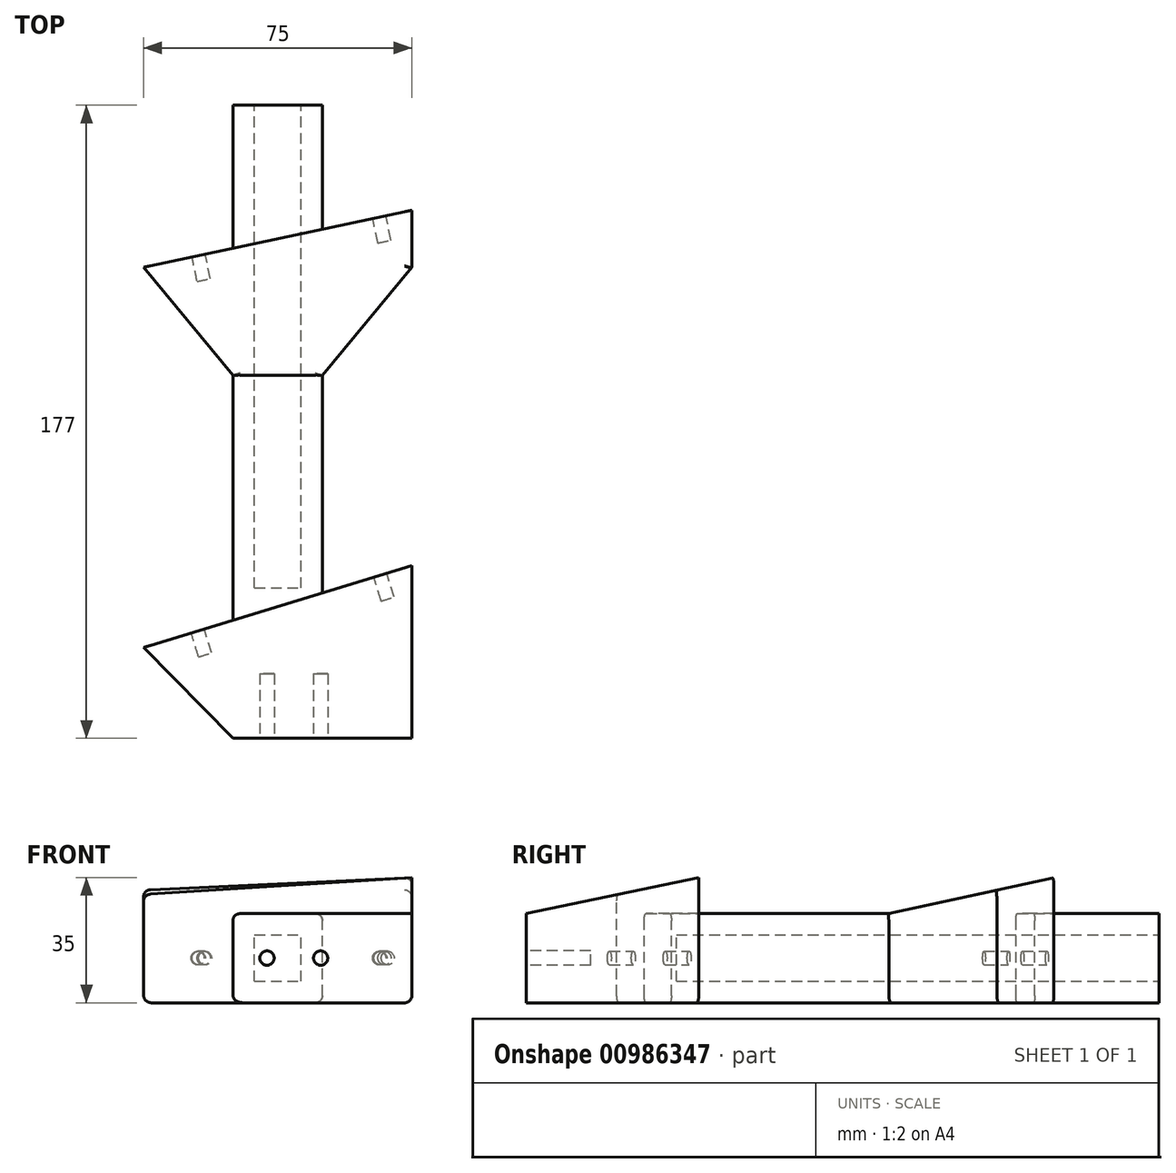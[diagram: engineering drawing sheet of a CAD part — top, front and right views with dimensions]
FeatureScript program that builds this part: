
annotation { "Feature Type Name" : "Feature", "Feature Type Description" : "" }
export const myFeature = defineFeature(function(context is Context, id is Id, definition is map)
    precondition{}
    {
        {
            var Q0;
            Q0=qCreatedBy(makeId("Top.planeOp"),FACE);
            var sketch = newSketch(context, id + "F0", { "sketchPlane" : qUnion([Q0])});
            skLineSegment(sketch, "E0.bottom", {"start": v(0, 0) * mm, "end": v(50, 0) * mm});
            skLineSegment(sketch, "E0.top", {"start": v(0, 33) * mm, "end": v(50, 33) * mm});
            skLineSegment(sketch, "E0.left", {"start": v(0, 0) * mm, "end": v(0, 33) * mm});
            skLineSegment(sketch, "E0.right", {"start": v(50, 0) * mm, "end": v(50, 33) * mm});
            skLineSegment(sketch, "E1", {"start": v(0, 33) * mm, "end": v(50, 48.29) * mm});
            skLineSegment(sketch, "E2", {"start": v(50, 33) * mm, "end": v(50, 48.29) * mm});
            skLineSegment(sketch, "E3", {"start": v(0, 33) * mm, "end": v(-25, 25.36) * mm});
            skLineSegment(sketch, "E4", {"start": v(-25, 25.36) * mm, "end": v(0, 0) * mm});
            skLineSegment(sketch, "E5", {"start": v(0, 33) * mm, "end": v(0, 137) * mm});
            skLineSegment(sketch, "E6", {"start": v(0, 137) * mm, "end": v(25, 137) * mm});
            skLineSegment(sketch, "E7", {"start": v(25, 137) * mm, "end": v(25, 0) * mm});
            skLineSegment(sketch, "E8", {"start": v(0, 137) * mm, "end": v(-25, 131.69) * mm});
            skLineSegment(sketch, "E9", {"start": v(-25, 131.69) * mm, "end": v(-25, 92.43) * mm});
            skLineSegment(sketch, "E10", {"start": v(-25, 131.69) * mm, "end": v(0, 101.46) * mm});
            skLineSegment(sketch, "E11", {"start": v(0, 137) * mm, "end": v(50, 147.63) * mm});
            skLineSegment(sketch, "E12", {"start": v(50, 147.63) * mm, "end": v(50, 131.69) * mm});
            skLineSegment(sketch, "E13", {"start": v(25, 101.46) * mm, "end": v(50, 131.69) * mm});
            skLineSegment(sketch, "E14", {"start": v(0, 137) * mm, "end": v(0, 177) * mm});
            skLineSegment(sketch, "E15", {"start": v(0, 177) * mm, "end": v(25, 177) * mm});
            skPoint(sketch, "E15.endSnap0", {"position": v(25, 142.31) * mm});
            skLineSegment(sketch, "E16", {"start": v(25, 177) * mm, "end": v(25, 137) * mm});
            skSolve(sketch);
        }
        {
            var Q0;
            Q0=qSketchRegion(id+"F0",true);
            extrude(context, id + "F1", {"entities" : qUnion([Q0]), "depth" : 25 * mm});
        }
        {
            var Q0;
            Q0=makeQuery(id+"F1.opExtrude","CAP_FACE",FACE,{"disambiguationData":[OSD([sQuery(id+"F0.wireOp",EDGE,"E0.bottom"),sQuery(id+"F0.wireOp",EDGE,"E0.right"),sQuery(id+"F0.wireOp",EDGE,"E1"),sQuery(id+"F0.wireOp",EDGE,"E2"),sQuery(id+"F0.wireOp",EDGE,"E3"),sQuery(id+"F0.wireOp",EDGE,"E4"),sQuery(id+"F0.wireOp",EDGE,"E5"),sQuery(id+"F0.wireOp",EDGE,"E7"),sQuery(id+"F0.wireOp",EDGE,"E8"),sQuery(id+"F0.wireOp",EDGE,"E10"),sQuery(id+"F0.wireOp",EDGE,"E11"),sQuery(id+"F0.wireOp",EDGE,"E12"),sQuery(id+"F0.wireOp",EDGE,"E13"),sQuery(id+"F0.wireOp",EDGE,"E14"),sQuery(id+"F0.wireOp",EDGE,"E15"),sQuery(id+"F0.wireOp",EDGE,"E16")])],"isStart":true});
            var sketch = newSketch(context, id + "F2", { "sketchPlane" : qUnion([Q0])});
            skLineSegment(sketch, "E17", {"start": v(25, -101.46) * mm, "end": v(0, -101.46) * mm});
            skLineSegment(sketch, "E18", {"start": v(0, -101.46) * mm, "end": v(-25, -131.69) * mm});
            skLineSegment(sketch, "E19", {"start": v(-25, -131.69) * mm, "end": v(50, -147.63) * mm});
            skLineSegment(sketch, "E20", {"start": v(50, -147.63) * mm, "end": v(50, -131.69) * mm});
            skLineSegment(sketch, "E21", {"start": v(50, -131.69) * mm, "end": v(25, -101.46) * mm});
            skSolve(sketch);
        }
        {
            var Q0;
            Q0=qSketchRegion(id+"F2",true);
            extrude(context, id + "F3", {"entities" : qUnion([Q0]), "operationType" : NewBodyOperationType.ADD, "depth" : 10 * mm});
        }
        {
            var Q0;
            Q0=makeQuery(id+"F1.opExtrude","SWEPT_FACE",FACE,{"disambiguationData":[OSD([sQuery(id+"F0.wireOp",EDGE,"E7")])]});
            var sketch = newSketch(context, id + "F4", { "sketchPlane" : qUnion([Q0])});
            skLineSegment(sketch, "E22", {"start": v(147.63, -10) * mm, "end": v(101.46, 0) * mm});
            skLineSegment(sketch, "E23", {"start": v(101.46, 0) * mm, "end": v(101.46, -21.14) * mm});
            skLineSegment(sketch, "E24", {"start": v(101.46, -21.14) * mm, "end": v(147.63, -10) * mm});
            skSolve(sketch);
        }
        {
            var Q0;
            Q0=qSketchRegion(id+"F4",true);
            extrude(context, id + "F5", {"entities" : qUnion([Q0]), "operationType" : NewBodyOperationType.REMOVE, "oppositeDirection" : true, "depth" : 163.4 * mm, "symmetric" : true});
        }
        {
            var Q0;
            {var subQ0=sQuery(id+"F0.wireOp",EDGE,"E13");var subQ1=sQuery(id+"F0.wireOp",EDGE,"E7");var subQ2=sQuery(id+"F0.wireOp",EDGE,"E5");var subQ3=sQuery(id+"F0.wireOp",EDGE,"E4");var subQ4=sQuery(id+"F0.wireOp",EDGE,"E0.bottom");var subQ5=sQuery(id+"F0.wireOp",EDGE,"E10");var subQ6=sQuery(id+"F0.wireOp",EDGE,"E2");var subQ7=sQuery(id+"F0.wireOp",EDGE,"E0.right");var subQ8=sQuery(id+"F0.wireOp",EDGE,"E1");var subQ9=sQuery(id+"F0.wireOp",EDGE,"E3");Q0=makeQuery(id+"F3.boolean.opBoolean","SPLIT",FACE,{"disambiguationData":[TD([makeQuery(id+"F1.opExtrude","SWEPT_FACE",FACE,{"disambiguationData":[OSD([subQ4])]})])],"derivedFrom":makeQuery(id+"F1.opExtrude","CAP_FACE",FACE,{"disambiguationData":[OSD([subQ4,subQ7,subQ8,subQ6,subQ9,subQ3,subQ2,subQ1,sQuery(id+"F0.wireOp",EDGE,"E8"),subQ5,sQuery(id+"F0.wireOp",EDGE,"E11"),sQuery(id+"F0.wireOp",EDGE,"E12"),subQ0,sQuery(id+"F0.wireOp",EDGE,"E14"),sQuery(id+"F0.wireOp",EDGE,"E15"),sQuery(id+"F0.wireOp",EDGE,"E16")])],"isStart":true})});}
            var sketch = newSketch(context, id + "F6", { "sketchPlane" : qUnion([Q0])});
            skLineSegment(sketch, "E25", {"start": v(50, 0) * mm, "end": v(50, -48.29) * mm});
            skLineSegment(sketch, "E26", {"start": v(50, -48.29) * mm, "end": v(-25, -25.36) * mm});
            skLineSegment(sketch, "E27", {"start": v(-25, -25.36) * mm, "end": v(0, 0) * mm});
            skLineSegment(sketch, "E28", {"start": v(0, 0) * mm, "end": v(50, 0) * mm});
            skSolve(sketch);
        }
        {
            var Q0;
            Q0=qSketchRegion(id+"F6",true);
            extrude(context, id + "F7", {"entities" : qUnion([Q0]), "operationType" : NewBodyOperationType.ADD, "depth" : 10 * mm});
        }
        {
            var Q0;
            Q0=makeQuery(id+"F7.boolean.opBoolean","MERGE",FACE,{"derivedFrom":[makeQuery(id+"F1.opExtrude","SWEPT_FACE",FACE,{"disambiguationData":[OSD([sQuery(id+"F0.wireOp",EDGE,"E0.right"),sQuery(id+"F0.wireOp",EDGE,"E2")])]}),makeQuery(id+"F7.opExtrude","SWEPT_FACE",FACE,{"disambiguationData":[OSD([sQuery(id+"F6.wireOp",EDGE,"E25")])]})]});
            var sketch = newSketch(context, id + "F8", { "sketchPlane" : qUnion([Q0])});
            skLineSegment(sketch, "E29", {"start": v(0, 0) * mm, "end": v(48.29, -10) * mm});
            skLineSegment(sketch, "E30", {"start": v(48.29, -10) * mm, "end": v(48.29, -39.53) * mm});
            skLineSegment(sketch, "E31", {"start": v(48.29, -39.53) * mm, "end": v(0, -39.53) * mm});
            skLineSegment(sketch, "E32", {"start": v(0, -39.53) * mm, "end": v(0, 0) * mm});
            skSolve(sketch);
        }
        {
            var Q0;
            Q0=qSketchRegion(id+"F8",true);
            extrude(context, id + "F9", {"entities" : qUnion([Q0]), "operationType" : NewBodyOperationType.REMOVE, "oppositeDirection" : true, "depth" : 92 * mm});
        }
        {
            var Q0;
            Q0=makeQuery(id+"F1.opExtrude","SWEPT_FACE",FACE,{"disambiguationData":[OSD([sQuery(id+"F0.wireOp",EDGE,"E15")])]});
            var sketch = newSketch(context, id + "F10", { "sketchPlane" : qUnion([Q0])});
            skLineSegment(sketch, "E33.bottom", {"start": v(-6, 19) * mm, "end": v(-19, 19) * mm});
            skLineSegment(sketch, "E33.top", {"start": v(-6, 6) * mm, "end": v(-19, 6) * mm});
            skLineSegment(sketch, "E33.left", {"start": v(-6, 19) * mm, "end": v(-6, 6) * mm});
            skLineSegment(sketch, "E33.right", {"start": v(-19, 19) * mm, "end": v(-19, 6) * mm});
            skPoint(sketch, "E33.middle", {"position": v(-12.5, 12.5) * mm});
            skPoint(sketch, "E33.middle.positionSnap0", {"position": v(-25, 12.5) * mm});
            skPoint(sketch, "E33.middle.positionSnap1", {"position": v(-12.5, 25) * mm});
            skPoint(sketch, "E33.centerSnap0", {"position": v(-25, 12.5) * mm});
            skPoint(sketch, "E33.centerSnap1", {"position": v(-12.5, 25) * mm});
            skSolve(sketch);
        }
        {
            var Q0;
            Q0=qSketchRegion(id+"F10",true);
            extrude(context, id + "F11", {"entities" : qUnion([Q0]), "operationType" : NewBodyOperationType.REMOVE, "oppositeDirection" : true, "depth" : 135 * mm});
        }
        {
            var Q0;
            Q0=makeQuery(id+"F1.opExtrude","CAP_FACE",FACE,{"disambiguationData":[OSD([sQuery(id+"F0.wireOp",EDGE,"E0.bottom"),sQuery(id+"F0.wireOp",EDGE,"E0.right"),sQuery(id+"F0.wireOp",EDGE,"E1"),sQuery(id+"F0.wireOp",EDGE,"E2"),sQuery(id+"F0.wireOp",EDGE,"E3"),sQuery(id+"F0.wireOp",EDGE,"E4"),sQuery(id+"F0.wireOp",EDGE,"E5"),sQuery(id+"F0.wireOp",EDGE,"E7"),sQuery(id+"F0.wireOp",EDGE,"E8"),sQuery(id+"F0.wireOp",EDGE,"E10"),sQuery(id+"F0.wireOp",EDGE,"E11"),sQuery(id+"F0.wireOp",EDGE,"E12"),sQuery(id+"F0.wireOp",EDGE,"E13"),sQuery(id+"F0.wireOp",EDGE,"E14"),sQuery(id+"F0.wireOp",EDGE,"E15"),sQuery(id+"F0.wireOp",EDGE,"E16")])],"isStart":false});
            cPlane(context, id + "F12", {"entities" : qUnion([Q0]), "cplaneType" : CPlaneType.OFFSET, "offset" : 25 * mm, "width" : 150 * mm, "height" : 150 * mm});
        }
        {
            var Q0;
            Q0=makeQuery(id+"F1.opExtrude","SWEPT_BODY",BODY,{"disambiguationData":[OSD([sQuery(id+"F0.wireOp",EDGE,"E0.bottom"),sQuery(id+"F0.wireOp",EDGE,"E0.right"),sQuery(id+"F0.wireOp",EDGE,"E1"),sQuery(id+"F0.wireOp",EDGE,"E2"),sQuery(id+"F0.wireOp",EDGE,"E3"),sQuery(id+"F0.wireOp",EDGE,"E4"),sQuery(id+"F0.wireOp",EDGE,"E5"),sQuery(id+"F0.wireOp",EDGE,"E7"),sQuery(id+"F0.wireOp",EDGE,"E8"),sQuery(id+"F0.wireOp",EDGE,"E10"),sQuery(id+"F0.wireOp",EDGE,"E11"),sQuery(id+"F0.wireOp",EDGE,"E12"),sQuery(id+"F0.wireOp",EDGE,"E13"),sQuery(id+"F0.wireOp",EDGE,"E14"),sQuery(id+"F0.wireOp",EDGE,"E15"),sQuery(id+"F0.wireOp",EDGE,"E16")])]});
            var Q1;
            Q1=qCreatedBy(id+"F12.planeOp",FACE);
            mirror(context, id + "F13", {"entities" : qUnion([Q0]), "mirrorPlane" : qUnion([Q1])});
        }
        {
            var Q0;
            Q0=qCreatedBy(id+"F12.planeOp",FACE);
            var sketch = newSketch(context, id + "F14", { "sketchPlane" : qUnion([Q0])});
            skLineSegment(sketch, "E34.bottom", {"start": v(-36.83, -9.19) * mm, "end": v(62.37, -9.19) * mm});
            skLineSegment(sketch, "E34.top", {"start": v(-36.83, 189.97) * mm, "end": v(62.37, 189.97) * mm});
            skLineSegment(sketch, "E34.left", {"start": v(-36.83, -9.19) * mm, "end": v(-36.83, 189.97) * mm});
            skLineSegment(sketch, "E34.right", {"start": v(62.37, -9.19) * mm, "end": v(62.37, 189.97) * mm});
            skSolve(sketch);
        }
        {
            var Q0;
            Q0=qSketchRegion(id+"F14",true);
            extrude(context, id + "F15", {"entities" : qUnion([Q0]), "operationType" : NewBodyOperationType.REMOVE, "oppositeDirection" : true, "depth" : 88 * mm});
        }
        {
            var Q0;
            Q0=makeQuery(id+"F13.opPattern","COPY",FACE,{"derivedFrom":makeQuery(id+"F3.boolean.opBoolean","MERGE",FACE,{"derivedFrom":[makeQuery(id+"F1.opExtrude","SWEPT_FACE",FACE,{"disambiguationData":[OSD([sQuery(id+"F0.wireOp",EDGE,"E8")])]}),makeQuery(id+"F1.opExtrude","SWEPT_FACE",FACE,{"disambiguationData":[OSD([sQuery(id+"F0.wireOp",EDGE,"E11")])]}),makeQuery(id+"F3.opExtrude","SWEPT_FACE",FACE,{"disambiguationData":[OSD([sQuery(id+"F2.wireOp",EDGE,"E19")])]})]}),"instanceName":"1"});
            var sketch = newSketch(context, id + "F16", { "sketchPlane" : qUnion([Q0])});
            skLineSegment(sketch, "E35", {"start": v(-2.93, 75) * mm, "end": v(-2.93, 87.5) * mm});
            skPoint(sketch, "E35.endSnap0", {"position": v(-28.48, 87.5) * mm});
            skLineSegment(sketch, "E36", {"start": v(-2.93, 87.5) * mm, "end": v(-18.63, 87.5) * mm});
            skLineSegment(sketch, "E37", {"start": v(-79.6, 75) * mm, "end": v(-79.6, 87.5) * mm});
            skLineSegment(sketch, "E38", {"start": v(-79.6, 87.5) * mm, "end": v(-70.3, 87.5) * mm});
            skCircle(sketch, "E39", {"center": v(-18.63, 87.5) * mm, "radius": 1.9 * mm});
            skCircle(sketch, "E40", {"center": v(-70.3, 87.5) * mm, "radius": 1.9 * mm});
            skSolve(sketch);
        }
        {
            var Q0;
            Q0=qSketchRegion(id+"F16",true);
            extrude(context, id + "F17", {"entities" : qUnion([Q0]), "operationType" : NewBodyOperationType.REMOVE, "oppositeDirection" : true, "depth" : 7 * mm});
        }
        {
            var Q0;
            Q0=makeQuery(id+"F13.opPattern","COPY",FACE,{"derivedFrom":makeQuery(id+"F7.boolean.opBoolean","MERGE",FACE,{"derivedFrom":[makeQuery(id+"F1.opExtrude","SWEPT_FACE",FACE,{"disambiguationData":[OSD([sQuery(id+"F0.wireOp",EDGE,"E1")])]}),makeQuery(id+"F1.opExtrude","SWEPT_FACE",FACE,{"disambiguationData":[OSD([sQuery(id+"F0.wireOp",EDGE,"E3")])]}),makeQuery(id+"F7.opExtrude","SWEPT_FACE",FACE,{"disambiguationData":[OSD([sQuery(id+"F6.wireOp",EDGE,"E26")])]})]}),"instanceName":"1"});
            var sketch = newSketch(context, id + "F18", { "sketchPlane" : qUnion([Q0])});
            skLineSegment(sketch, "E41", {"start": v(16.5, 75) * mm, "end": v(16.5, 87.5) * mm});
            skPoint(sketch, "E41.endSnap0", {"position": v(-9.65, 87.5) * mm});
            skLineSegment(sketch, "E42", {"start": v(16.5, 87.5) * mm, "end": v(0.7, 87.5) * mm});
            skLineSegment(sketch, "E43", {"start": v(-61.93, 75) * mm, "end": v(-61.93, 87.5) * mm});
            skLineSegment(sketch, "E44", {"start": v(-61.93, 87.5) * mm, "end": v(-52.73, 87.5) * mm});
            skCircle(sketch, "E45", {"center": v(0.7, 87.5) * mm, "radius": 1.9 * mm});
            skCircle(sketch, "E46", {"center": v(-52.73, 87.5) * mm, "radius": 1.9 * mm});
            skSolve(sketch);
        }
        {
            var Q0;
            Q0=qSketchRegion(id+"F18",true);
            extrude(context, id + "F19", {"entities" : qUnion([Q0]), "operationType" : NewBodyOperationType.REMOVE, "oppositeDirection" : true, "depth" : 7 * mm});
        }
        {
            var Q0;
            Q0=makeQuery(id+"F13.opPattern","COPY",FACE,{"derivedFrom":makeQuery(id+"F7.boolean.opBoolean","MERGE",FACE,{"derivedFrom":[makeQuery(id+"F1.opExtrude","SWEPT_FACE",FACE,{"disambiguationData":[OSD([sQuery(id+"F0.wireOp",EDGE,"E0.bottom")])]}),makeQuery(id+"F7.opExtrude","SWEPT_FACE",FACE,{"disambiguationData":[OSD([sQuery(id+"F6.wireOp",EDGE,"E28")])]})]}),"instanceName":"1"});
            var sketch = newSketch(context, id + "F20", { "sketchPlane" : qUnion([Q0])});
            skLineSegment(sketch, "E47", {"start": v(0, 87.5) * mm, "end": v(9.5, 87.5) * mm});
            skLineSegment(sketch, "E48", {"start": v(9.5, 87.5) * mm, "end": v(24.5, 87.5) * mm});
            skCircle(sketch, "E49", {"center": v(9.5, 87.5) * mm, "radius": 2 * mm});
            skCircle(sketch, "E50", {"center": v(24.5, 87.5) * mm, "radius": 2 * mm});
            skSolve(sketch);
        }
        {
            var Q0;
            Q0=qSketchRegion(id+"F20",true);
            extrude(context, id + "F21", {"entities" : qUnion([Q0]), "operationType" : NewBodyOperationType.REMOVE, "oppositeDirection" : true, "depth" : 18 * mm});
        }
        {
            var Q0;
            Q0=makeQuery(id+"F13.opPattern","COPY",EDGE,{"derivedFrom":makeQuery(id+"F1.opExtrude","CAP_EDGE",EDGE,{"disambiguationData":[OSD([sQuery(id+"F0.wireOp",EDGE,"E7")])],"isStart":true}),"instanceName":"1"});
            var Q1;
            Q1=makeQuery(id+"F13.opPattern","COPY",EDGE,{"derivedFrom":makeQuery(id+"F1.opExtrude","CAP_EDGE",EDGE,{"disambiguationData":[OSD([sQuery(id+"F0.wireOp",EDGE,"E5")])],"isStart":true}),"instanceName":"1"});
            var Q2;
            Q2=makeQuery(id+"F13.opPattern","COPY",EDGE,{"derivedFrom":makeQuery(id+"F1.opExtrude","CAP_EDGE",EDGE,{"disambiguationData":[OSD([sQuery(id+"F0.wireOp",EDGE,"E7")])],"isStart":false}),"instanceName":"1"});
            var Q3;
            Q3=makeQuery(id+"F13.opPattern","COPY",EDGE,{"derivedFrom":makeQuery(id+"F1.opExtrude","CAP_EDGE",EDGE,{"disambiguationData":[OSD([sQuery(id+"F0.wireOp",EDGE,"E5")])],"isStart":false}),"instanceName":"1"});
            var Q4;
            Q4=makeQuery(id+"F13.opPattern","COPY",EDGE,{"derivedFrom":makeQuery(id+"F1.opExtrude","CAP_EDGE",EDGE,{"disambiguationData":[OSD([sQuery(id+"F0.wireOp",EDGE,"E0.right"),sQuery(id+"F0.wireOp",EDGE,"E2")])],"isStart":false}),"instanceName":"1"});
            var Q5;
            Q5=makeQuery(id+"F13.opPattern","COPY",EDGE,{"derivedFrom":makeQuery(id+"F9.boolean.opBoolean","COPY",EDGE,{"derivedFrom":makeQuery(id+"F9.opExtrude","CAP_EDGE",EDGE,{"disambiguationData":[OSD([sQuery(id+"F8.wireOp",EDGE,"E29")])],"isStart":true})}),"instanceName":"1"});
            var Q6;
            Q6=makeQuery(id+"F13.opPattern","COPY",EDGE,{"derivedFrom":makeQuery(id+"F1.opExtrude","CAP_EDGE",EDGE,{"disambiguationData":[OSD([sQuery(id+"F0.wireOp",EDGE,"E4")])],"isStart":false}),"instanceName":"1"});
            var Q7;
            Q7=makeQuery(id+"F13.opPattern","COPY",EDGE,{"derivedFrom":makeQuery(id+"F9.boolean.opBoolean","INTERSECT",EDGE,{"derivedFrom":[makeQuery(id+"F7.boolean.opBoolean","MERGE",FACE,{"derivedFrom":[makeQuery(id+"F1.opExtrude","SWEPT_FACE",FACE,{"disambiguationData":[OSD([sQuery(id+"F0.wireOp",EDGE,"E4")])]}),makeQuery(id+"F7.opExtrude","SWEPT_FACE",FACE,{"disambiguationData":[OSD([sQuery(id+"F6.wireOp",EDGE,"E27")])]})]}),makeQuery(id+"F9.opExtrude","SWEPT_FACE",FACE,{"disambiguationData":[OSD([sQuery(id+"F8.wireOp",EDGE,"E29")])]})]}),"instanceName":"1"});
            var Q8;
            Q8=makeQuery(id+"F13.opPattern","COPY",EDGE,{"derivedFrom":makeQuery(id+"F1.opExtrude","CAP_EDGE",EDGE,{"disambiguationData":[OSD([sQuery(id+"F0.wireOp",EDGE,"E10")])],"isStart":false}),"instanceName":"1"});
            var Q9;
            Q9=makeQuery(id+"F13.opPattern","COPY",EDGE,{"derivedFrom":makeQuery(id+"F5.boolean.opBoolean","INTERSECT",EDGE,{"derivedFrom":[makeQuery(id+"F3.boolean.opBoolean","MERGE",FACE,{"derivedFrom":[makeQuery(id+"F1.opExtrude","SWEPT_FACE",FACE,{"disambiguationData":[OSD([sQuery(id+"F0.wireOp",EDGE,"E10")])]}),makeQuery(id+"F3.opExtrude","SWEPT_FACE",FACE,{"disambiguationData":[OSD([sQuery(id+"F2.wireOp",EDGE,"E18")])]})]}),makeQuery(id+"F5.opExtrude","SWEPT_FACE",FACE,{"disambiguationData":[OSD([sQuery(id+"F4.wireOp",EDGE,"E22")])]})]}),"instanceName":"1"});
            var Q10;
            Q10=makeQuery(id+"F13.opPattern","COPY",EDGE,{"derivedFrom":makeQuery(id+"F1.opExtrude","CAP_EDGE",EDGE,{"disambiguationData":[OSD([sQuery(id+"F0.wireOp",EDGE,"E13")])],"isStart":false}),"instanceName":"1"});
            var Q11;
            Q11=makeQuery(id+"F13.opPattern","COPY",EDGE,{"derivedFrom":makeQuery(id+"F5.boolean.opBoolean","INTERSECT",EDGE,{"derivedFrom":[makeQuery(id+"F3.boolean.opBoolean","MERGE",FACE,{"derivedFrom":[makeQuery(id+"F1.opExtrude","SWEPT_FACE",FACE,{"disambiguationData":[OSD([sQuery(id+"F0.wireOp",EDGE,"E13")])]}),makeQuery(id+"F3.opExtrude","SWEPT_FACE",FACE,{"disambiguationData":[OSD([sQuery(id+"F2.wireOp",EDGE,"E21")])]})]}),makeQuery(id+"F5.opExtrude","SWEPT_FACE",FACE,{"disambiguationData":[OSD([sQuery(id+"F4.wireOp",EDGE,"E22")])]})]}),"instanceName":"1"});
            var Q12;
            Q12=makeQuery(id+"F13.opPattern","COPY",EDGE,{"derivedFrom":makeQuery(id+"F5.boolean.opBoolean","INTERSECT",EDGE,{"derivedFrom":[makeQuery(id+"F3.boolean.opBoolean","MERGE",FACE,{"derivedFrom":[makeQuery(id+"F1.opExtrude","SWEPT_FACE",FACE,{"disambiguationData":[OSD([sQuery(id+"F0.wireOp",EDGE,"E12")])]}),makeQuery(id+"F3.opExtrude","SWEPT_FACE",FACE,{"disambiguationData":[OSD([sQuery(id+"F2.wireOp",EDGE,"E20")])]})]}),makeQuery(id+"F5.opExtrude","SWEPT_FACE",FACE,{"disambiguationData":[OSD([sQuery(id+"F4.wireOp",EDGE,"E22")])]})]}),"instanceName":"1"});
            var Q13;
            Q13=makeQuery(id+"F13.opPattern","COPY",EDGE,{"derivedFrom":makeQuery(id+"F1.opExtrude","CAP_EDGE",EDGE,{"disambiguationData":[OSD([sQuery(id+"F0.wireOp",EDGE,"E12")])],"isStart":false}),"instanceName":"1"});
            var Q14;
            Q14=makeQuery(id+"F13.opPattern","COPY",EDGE,{"derivedFrom":makeQuery(id+"F1.opExtrude","CAP_EDGE",EDGE,{"disambiguationData":[OSD([sQuery(id+"F0.wireOp",EDGE,"E16")])],"isStart":true}),"instanceName":"1"});
            var Q15;
            Q15=makeQuery(id+"F13.opPattern","COPY",EDGE,{"derivedFrom":makeQuery(id+"F1.opExtrude","CAP_EDGE",EDGE,{"disambiguationData":[OSD([sQuery(id+"F0.wireOp",EDGE,"E14")])],"isStart":false}),"instanceName":"1"});
            var Q16;
            Q16=makeQuery(id+"F13.opPattern","COPY",EDGE,{"derivedFrom":makeQuery(id+"F1.opExtrude","CAP_EDGE",EDGE,{"disambiguationData":[OSD([sQuery(id+"F0.wireOp",EDGE,"E16")])],"isStart":false}),"instanceName":"1"});
            var Q17;
            Q17=makeQuery(id+"F13.opPattern","COPY",EDGE,{"derivedFrom":makeQuery(id+"F1.opExtrude","CAP_EDGE",EDGE,{"disambiguationData":[OSD([sQuery(id+"F0.wireOp",EDGE,"E14")])],"isStart":true}),"instanceName":"1"});
            fillet(context, id + "F22", {"entities" : qUnion([Q0, Q1, Q2, Q3, Q4, Q5, Q6, Q7, Q8, Q9, Q10, Q11, Q12, Q13, Q14, Q15, Q16, Q17]), "radius" : 2 * mm, "tangentPropagation" : true, "allowEdgeOverflow" : false});
        }
    });
